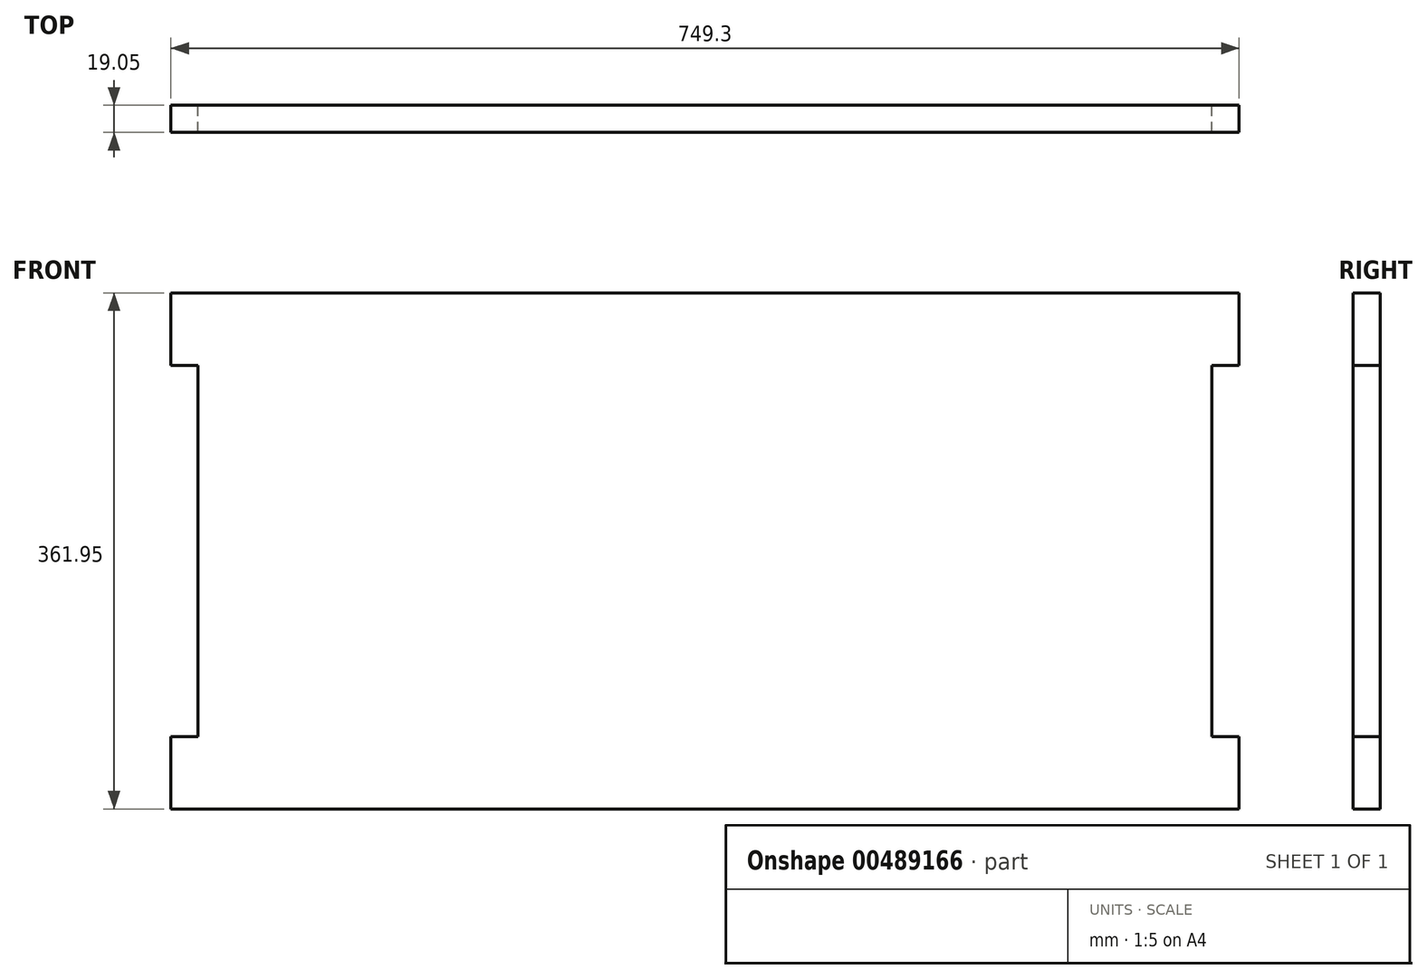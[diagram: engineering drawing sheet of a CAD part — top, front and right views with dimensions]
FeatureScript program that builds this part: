
annotation { "Feature Type Name" : "Feature", "Feature Type Description" : "" }
export const myFeature = defineFeature(function(context is Context, id is Id, definition is map)
    precondition{}
    {
        {
            var Q0;
            Q0=qCreatedBy(makeId("Front.planeOp"),FACE);
            var sketch = newSketch(context, id + "F0", { "sketchPlane" : qUnion([Q0])});
            skLineSegment(sketch, "E0", {"start": v(-749.3, 321.53) * mm, "end": v(-749.3, 270.73) * mm});
            skLineSegment(sketch, "E1", {"start": v(-749.3, 270.73) * mm, "end": v(-730.25, 270.73) * mm});
            skLineSegment(sketch, "E2", {"start": v(-730.25, 270.73) * mm, "end": v(-730.25, 10.38) * mm});
            skLineSegment(sketch, "E3", {"start": v(-730.25, 10.38) * mm, "end": v(-749.3, 10.38) * mm});
            skLineSegment(sketch, "E4", {"start": v(-749.3, 10.38) * mm, "end": v(-749.3, -40.42) * mm});
            skLineSegment(sketch, "E5", {"start": v(-749.3, -40.42) * mm, "end": v(0, -40.42) * mm});
            skLineSegment(sketch, "E6", {"start": v(-749.3, 321.53) * mm, "end": v(0, 321.53) * mm});
            skLineSegment(sketch, "E7", {"start": v(-19.05, 270.73) * mm, "end": v(-19.05, 10.38) * mm});
            skLineSegment(sketch, "E8", {"start": v(-19.05, 10.38) * mm, "end": v(0, 10.38) * mm});
            skLineSegment(sketch, "E9", {"start": v(0, 10.38) * mm, "end": v(0, -40.42) * mm});
            skLineSegment(sketch, "E10", {"start": v(-19.05, 270.73) * mm, "end": v(0, 270.73) * mm});
            skLineSegment(sketch, "E11", {"start": v(0, 270.73) * mm, "end": v(0, 321.53) * mm});
            skSolve(sketch);
        }
        {
            var Q0;
            Q0=makeQuery(id+"F0.imprint","IMPRINT",FACE,{"disambiguationData":[TD([[makeQuery(id+"F0.imprint","IMPRINT",EDGE,{"derivedFrom":sQuery(id+"F0.wireOp",EDGE,"E0")}),1.0]])]});
            extrude(context, id + "F1", {"entities" : qUnion([Q0]), "depth" : 19.05 * mm});
        }
    });
